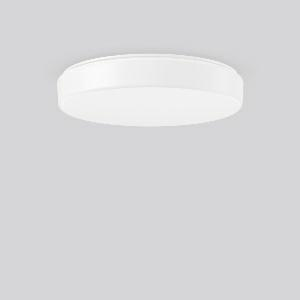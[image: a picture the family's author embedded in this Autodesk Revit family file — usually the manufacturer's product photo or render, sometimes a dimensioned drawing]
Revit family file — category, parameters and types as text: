
# Revit family: flat_polymero_kreis_672392_002_89_1398
name_source: partatom
category: Lighting Fixtures
units: mm (PartAtom-declared; Revit-internal decimal feet)

## family parameters
Cut with Voids When Loaded = No
Host = Face
Light Source = No
Part Type = Normal
Room Calculation Point = No
Round Connector Dimension = Use Diameter
Shared = No

## types (1)
- FLAT POLYMERO KREIS (1 x LED Modul 830, 2500 lm, 3000)
    Apparent Load = 24 VA
    CIE Flux Codes = 42 72 91 84 100
    Color Rendering = 80
    Color Temperature = 3000
    Default Elevation = 1800 mm
    Description = Series: FLAT POLYMERO KREIS
Decorative round surface-mounted luminaire. For escape route illumination. Base: metal, powder-coated. Diffuser made of non-yellowing plastic (PMMA), opal. Diffuser fastening: patented push system. Suitable for Ceiling mounting, Wall (surface). Driver integrated. Suitable for connection to central battery systems. With AC Control monitoring module for LUXIFAIR central battery units. 
Colour: white
Diameter: 515 mm
Height: 98 mm
Weight: 2.86 kg
Operating mode: Non-maintained power mode and maintained power mode
Lamp: LED
Socket: without socket
Colour temperature: 3000K
Colour rendering index (CRI): 80
System power: 24 W
Rated luminous flux: 2500 lm
Luminous flux, emergency: 520 lm
System power, emergency: 6.9 W
Control gear: Regulated power supply
Protection class: I
Type of protection: IP 40
    Height = 98 mm
    Lamp = 1 x LED Modul 830
    Lamp Light Flux = 2500 lm
    Lamp count = 1
    Length = 515 mm
    Lifetime = 50000 h
    Luminous efficacy = 104 lm/W
    Manufacturer = RZB
    ModVariant = No
    Model = 672392.002.89
    Mounting Place = Ceiling, Wall
    Mounting Type = Surface mounted
    Number of Poles = 1
    OnlyDefault = Yes
    Power Factor = 1
    Product Name = FLAT POLYMERO KREIS
    Product group = Surface mounted ceiling and wall luminaires
    ProductGroupID = 305
    Protection Class = Protection class I
    Protection Degree = IP 40
    RLX_Detail_Level = 1
    RLX_Emergency_Light_Flux = 520 lm
    RLX_Emergency_Type = 3
    RLX_Emergency_Type_DB = Yes
    RlxData = <blob elided: 57101 chars, md5=df83543a>
    Socket = socket
    Standby Power = 0 W
    System Light Flux = 2500 lm
    System Power = 24 W
    Type Comments = Product without accessories
    Type Image = 311604.862.79.jpg
    URL = http://relux.com
    VarID = ---
    Voltage = 230 V
    Voltage Range = 220-240 V
    Weight = 0.00 kg
    Width = 0 mm  [stored 0 ft]

note: [stored X ft] marks values corroborated as IEEE doubles in the binary element streams (Revit-internal decimal feet)

## geometry (parser evidence)
native form markers: Blend x4, Sweep x13
no freeform markers — native parametric forms only
